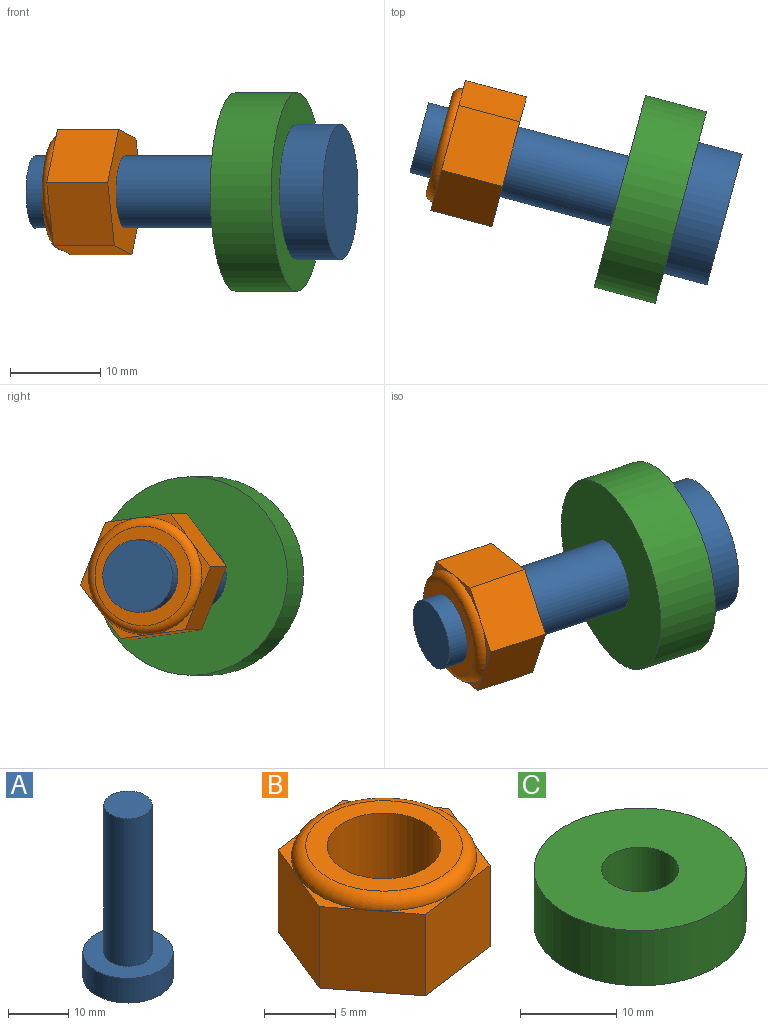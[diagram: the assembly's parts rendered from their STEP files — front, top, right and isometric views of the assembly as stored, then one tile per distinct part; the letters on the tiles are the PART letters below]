
ASSEMBLY  parts=3 mates=2
PART A: 5 faces, bbox 15x15x35 mm
  f0: cylinder r=4mm len=30mm, axis (0,0,-1), area 754mm2, adj f1,f4
  f1: plane 8x8mm, normal (0,0,1), area 50.3mm2, adj f0
  f2: cylinder r=7.5mm len=15mm, axis (0,0,1), area 235.6mm2, adj f3,f4
  f3: plane 15x15mm, normal (0,0,-1), area 176.7mm2, adj f2
  f4: plane 15x15mm, normal (0,0,1), area 126.4mm2, adj f0,f2
PART B: 16 faces, bbox 14.9x14.1x8 mm
  f0: plane 7x6.94mm, normal (-0.92,0.38,0), area 52.5mm2, adj f1,f2,f8,f11,f14
  f1: plane 7x5.94mm, normal (-0.79,-0.61,0), area 52.5mm2, adj f0,f4,f8,f10,f14
  f2: plane 7.44x7mm, normal (-0.13,0.99,0), area 52.5mm2, adj f0,f3,f8,f11,f13
  f3: plane 7x5.94mm, normal (0.79,0.61,0), area 52.5mm2, adj f2,f5,f8,f9,f13
  f4: plane 7.44x7mm, normal (0.13,-0.99,0), area 52.5mm2, adj f1,f5,f8,f10,f12
  f5: plane 7x6.94mm, normal (0.92,-0.38,0), area 52.5mm2, adj f3,f4,f8,f9,f12
  f6: cylinder r=4mm len=8mm, axis (0,0,-1), area 201.1mm2, adj f7,f8
  f7: plane 11x11mm, normal (0,0,1), area 44.8mm2, adj f6,f15
  f8: plane 14.88x13.88mm, normal (0,0,-1), area 96.1mm2, adj f0,f1,f2,f3,f4,f5,f6
  f9: plane 6.44x2.29mm, normal (0,0,1), area 2.3mm2, adj f3,f5,f15
  f10: plane 6.01x2.97mm, normal (0,0,1), area 2.3mm2, adj f1,f4,f15
  f11: plane 5.15x3.97mm, normal (0,0,1), area 2.3mm2, adj f0,f2,f15
  f12: plane 5.15x3.97mm, normal (0,0,1), area 2.3mm2, adj f4,f5,f15
  f13: plane 6.01x2.97mm, normal (0,0,1), area 2.3mm2, adj f2,f3,f15
  f14: plane 6.44x2.29mm, normal (0,0,1), area 2.3mm2, adj f0,f1,f15
  f15: torus R=5.5mm, axis (0,0,1), area 60.6mm2, adj f7,f9,f10,f11,f12,f13,f14
PART C: 4 faces, bbox 22x22x7 mm
  f0: cylinder r=4mm len=8mm, axis (0,0,-1), area 175.9mm2, adj f2,f3
  f1: cylinder r=11mm len=22mm, axis (0,0,-1), area 483.8mm2, adj f2,f3
  f2: plane 22x22mm, normal (0,0,1), area 329.9mm2, adj f0,f1
  f3: plane 22x22mm, normal (0,0,-1), area 329.9mm2, adj f0,f1
PLACE A rot(axis=(-0.13,-0.98,-0.13),91deg) t=(65.43,-38.78,-33.47)mm
PLACE B rot(axis=(-0.68,-0.52,0.52),111.8deg) t=(62.67,27.03,-123.91)mm
PLACE C rot(axis=(-0.68,-0.52,0.52),111.8deg) t=(72.11,-13.84,-95.06)mm
MATE cylindrical B.f6 <-> A.f0  axis (0.97,-0.26,0) through (39.46,-28.66,-91.25)mm
MATE cylindrical C.f0 <-> A.f0  axis (0.97,-0.26,0) through (59.46,-34.02,-91.25)mm
